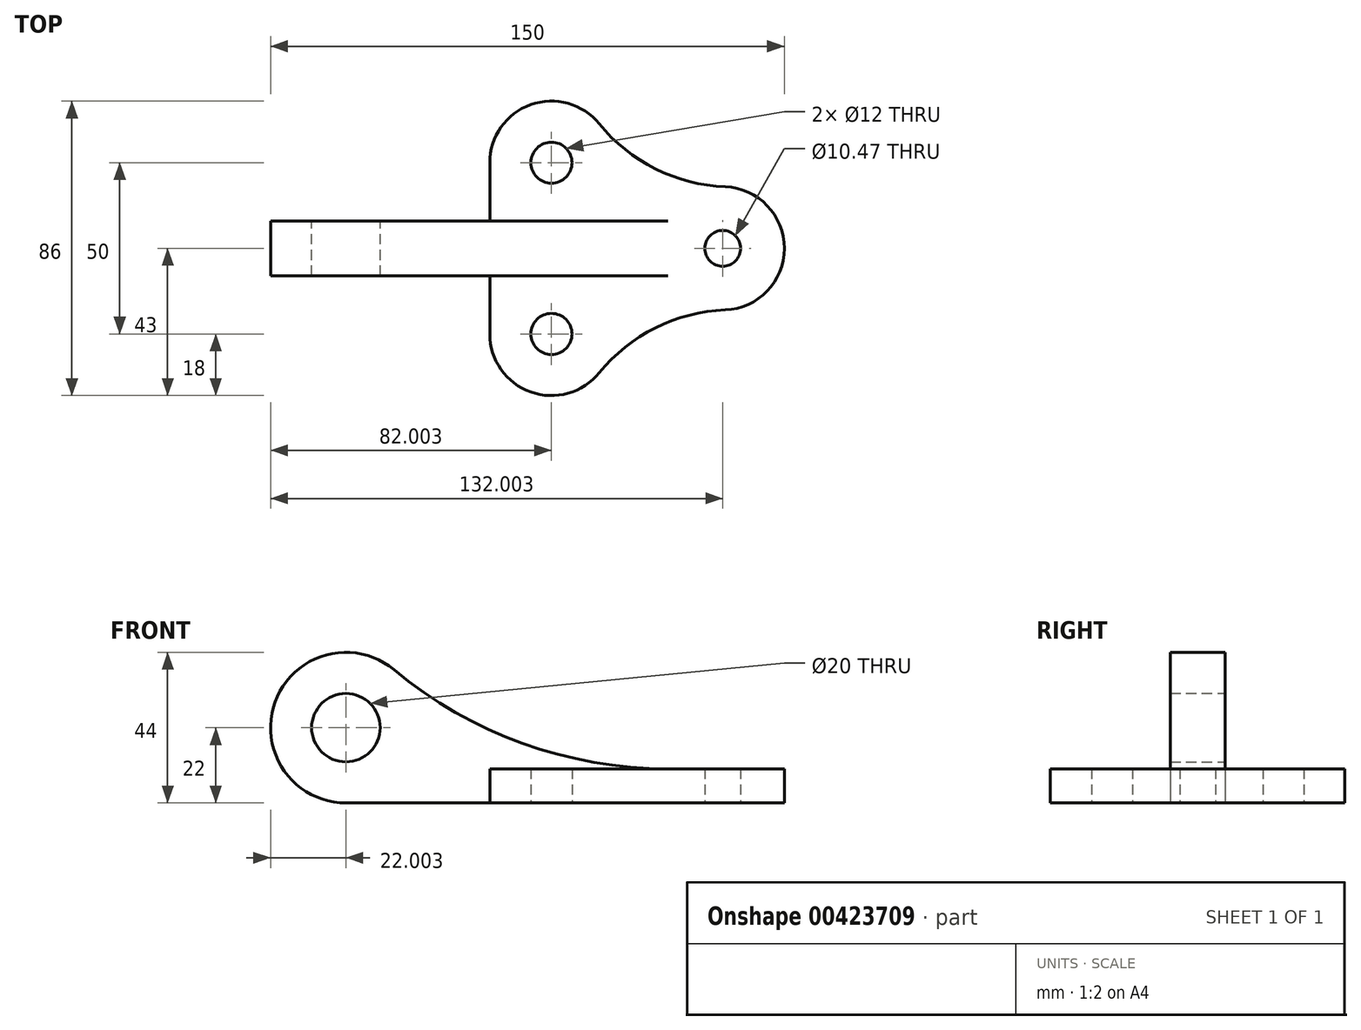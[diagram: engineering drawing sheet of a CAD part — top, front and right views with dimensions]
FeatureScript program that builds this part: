
annotation { "Feature Type Name" : "Feature", "Feature Type Description" : "" }
export const myFeature = defineFeature(function(context is Context, id is Id, definition is map)
    precondition{}
    {
        {
            var Q0;
            Q0=qCreatedBy(makeId("Top.planeOp"),FACE);
            var sketch = newSketch(context, id + "F0", { "sketchPlane" : qUnion([Q0])});
            skCircle(sketch, "E0", {"center": v(40.83, 0) * mm, "radius": 5.24 * mm});
            skCircle(sketch, "E1", {"center": v(-9.17, 25) * mm, "radius": 6 * mm});
            skCircle(sketch, "E2", {"center": v(-9.17, -25) * mm, "radius": 6 * mm});
            skArc(sketch, "E3", {"start": v(41.55, -17.99) * mm, "mid": v(58.83, 0) * mm, "end": v(41.55, 17.99) * mm});
            skArc(sketch, "E4", {"start": v(4.79, 36.37) * mm, "mid": v(-15.2, 41.96) * mm, "end": v(-27.17, 25) * mm});
            skArc(sketch, "E5", {"start": v(-27.17, -25) * mm, "mid": v(-15.2, -41.96) * mm, "end": v(4.79, -36.37) * mm});
            skArc(sketch, "E6", {"start": v(41.55, -17.99) * mm, "mid": v(21.2, -23.22) * mm, "end": v(4.79, -36.37) * mm});
            skPoint(sketch, "E6.first.point", {"position": v(4.79, -36.37) * mm});
            skPoint(sketch, "E6.second.point", {"position": v(61.44, -21.25) * mm});
            skPoint(sketch, "E6.third.point", {"position": v(90.04, -86.36) * mm});
            skArc(sketch, "E7", {"start": v(4.79, 36.37) * mm, "mid": v(21.2, 23.22) * mm, "end": v(41.55, 17.99) * mm});
            skPoint(sketch, "E7.first.point", {"position": v(4.79, 36.37) * mm});
            skPoint(sketch, "E7.second.point", {"position": v(41.55, 17.99) * mm});
            skPoint(sketch, "E7.third.point", {"position": v(86.4, 93.7) * mm});
            skLineSegment(sketch, "E8", {"start": v(-27.17, 25) * mm, "end": v(-27.17, -25) * mm});
            skSolve(sketch);
        }
        {
            var Q0;
            Q0=makeQuery(id+"F0.imprint","IMPRINT",FACE,{"disambiguationData":[TD([[makeQuery(id+"F0.imprint","IMPRINT",EDGE,{"derivedFrom":sQuery(id+"F0.wireOp",EDGE,"E0")}),-1.0]])]});
            extrude(context, id + "F1", {"entities" : qUnion([Q0]), "depth" : 10 * mm});
        }
        {
            var Q0;
            Q0=qCreatedBy(makeId("Front.planeOp"),FACE);
            var sketch = newSketch(context, id + "F2", { "sketchPlane" : qUnion([Q0])});
            skCircle(sketch, "E9", {"center": v(-69.17, 22) * mm, "radius": 10 * mm});
            skLineSegment(sketch, "E10.0", {"start": v(35.6, 10) * mm, "end": v(46.07, 10) * mm, "construction": true});
            skLineSegment(sketch, "E11", {"start": v(-69.17, 0) * mm, "end": v(0, 0) * mm});
            skArc(sketch, "E12", {"start": v(-55.1, 38.91) * mm, "mid": v(-89.86, 29.48) * mm, "end": v(-69.17, 0) * mm});
            skLineSegment(sketch, "E13.0.0", {"start": v(-27.17, 0) * mm, "end": v(4.79, 0) * mm, "construction": true});
            skArc(sketch, "E14", {"start": v(-55.1, 38.91) * mm, "mid": v(-17.65, 17.45) * mm, "end": v(24.85, 10) * mm});
            skPoint(sketch, "E14.first.point", {"position": v(-55.1, 38.91) * mm});
            skPoint(sketch, "E14.second.point", {"position": v(24.85, 10) * mm});
            skPoint(sketch, "E14.third.point", {"position": v(146.52, 106.33) * mm});
            skPoint(sketch, "E15.orphan", {"position": v(-79.88, 0) * mm});
            skPoint(sketch, "E16.start.orphan", {"position": v(40.83, 10) * mm});
            skLineSegment(sketch, "E17", {"start": v(24.85, 10) * mm, "end": v(24.85, 0) * mm});
            skLineSegment(sketch, "E18", {"start": v(24.85, 0) * mm, "end": v(-27.17, 0) * mm});
            skSolve(sketch);
        }
        {
            var Q0;
            Q0 = qSketchRegion(id + "F2", true);
            extrude(context, id + "F3", {"entities" : qUnion([Q0]), "operationType" : NewBodyOperationType.ADD, "endBound" : BoundingType.SYMMETRIC, "depth" : 16 * mm});
        }
    });
